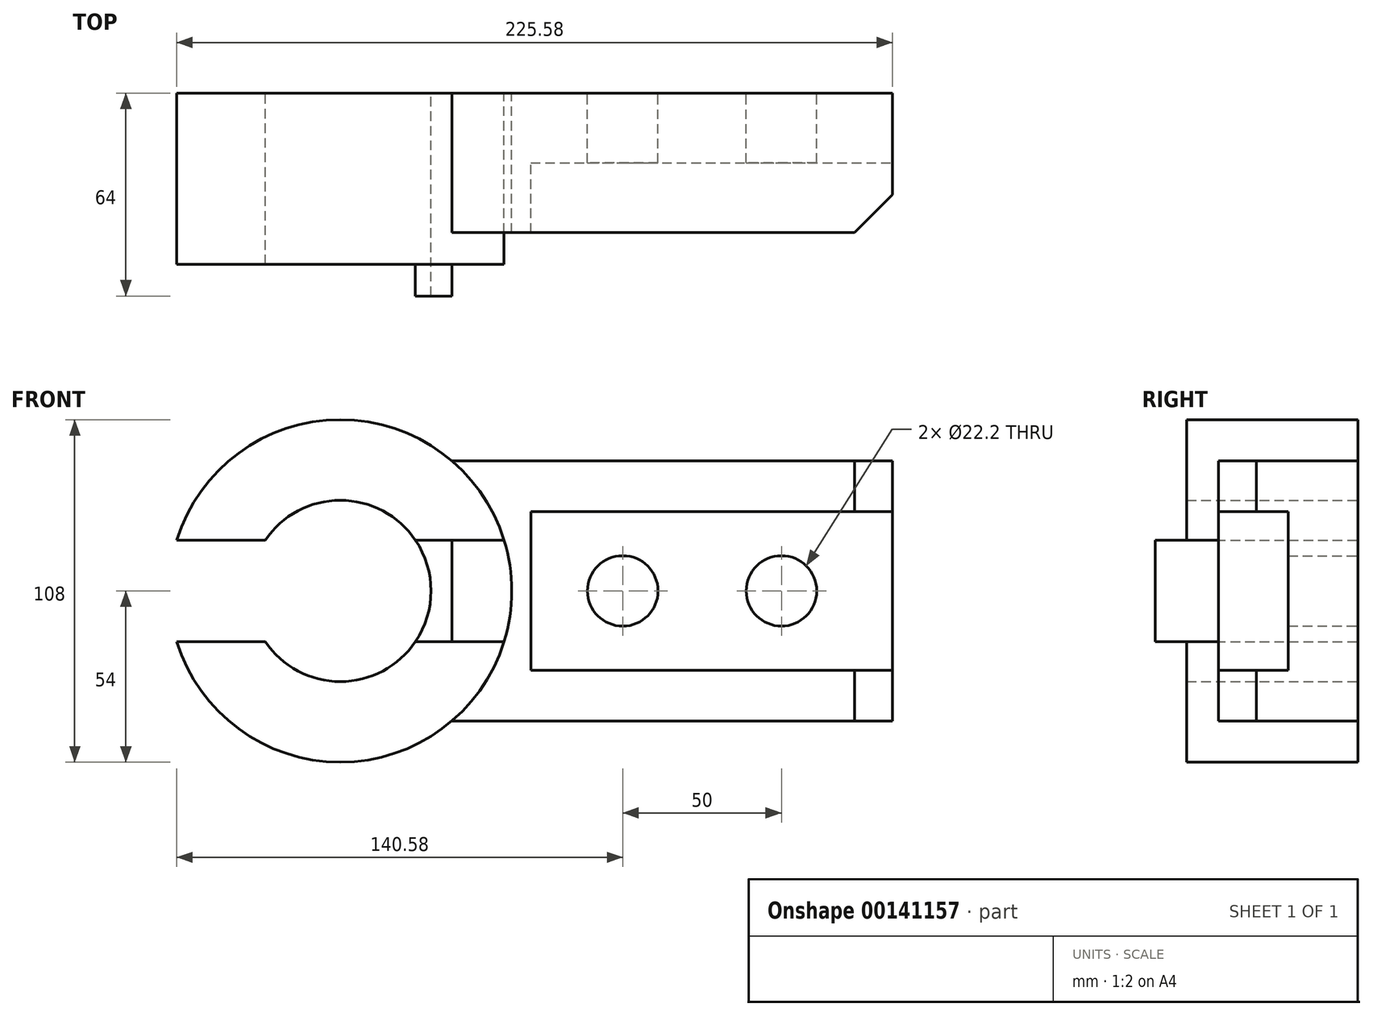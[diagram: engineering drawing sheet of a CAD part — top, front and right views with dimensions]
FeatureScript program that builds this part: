
annotation { "Feature Type Name" : "Feature", "Feature Type Description" : "" }
export const myFeature = defineFeature(function(context is Context, id is Id, definition is map)
    precondition{}
    {
        {
            var Q0;
            Q0=qCreatedBy(makeId("Front.planeOp"),FACE);
            var sketch = newSketch(context, id + "F0", { "sketchPlane" : qUnion([Q0])});
            skCircle(sketch, "E0", {"center": v(0, 41) * mm, "radius": 54 * mm});
            skLineSegment(sketch, "E1.bottom", {"start": v(35.14, 82) * mm, "end": v(174, 82) * mm});
            skLineSegment(sketch, "E1.top", {"start": v(35.14, 0) * mm, "end": v(174, 0) * mm});
            skLineSegment(sketch, "E1.left", {"start": v(35.14, 82) * mm, "end": v(35.14, 0) * mm});
            skLineSegment(sketch, "E1.right", {"start": v(174, 82) * mm, "end": v(174, 0) * mm});
            skCircle(sketch, "E2", {"center": v(0, 41) * mm, "radius": 28.57 * mm});
            skCircle(sketch, "E3", {"center": v(89, 41) * mm, "radius": 11.1 * mm});
            skCircle(sketch, "E4", {"center": v(139, 41) * mm, "radius": 11.1 * mm});
            skLineSegment(sketch, "E5.bottom", {"start": v(-51.58, 57) * mm, "end": v(51.58, 57) * mm});
            skLineSegment(sketch, "E5.top", {"start": v(-51.58, 25) * mm, "end": v(51.58, 25) * mm});
            skArc(sketch, "E6", {"start": v(-51.58, 57) * mm, "mid": v(-54, 41) * mm, "end": v(-51.58, 25) * mm});
            skArc(sketch, "E7", {"start": v(51.58, 25) * mm, "mid": v(54, 41) * mm, "end": v(51.58, 57) * mm});
            skSolve(sketch);
        }
        {
            var Q0;
            {var subQ1=sQuery(id+"F0.wireOp",EDGE,"E1.bottom");Q0=makeQuery(id+"F0.imprint","IMPRINT",FACE,{"disambiguationData":[TD([[makeQuery(id+"F0.imprint","IMPRINT",EDGE,{"derivedFrom":subQ1}),-1.0]])]});}
            extrude(context, id + "F1", {"entities" : qUnion([Q0]), "depth" : 44 * mm});
        }
        {
            var Q0;
            {var subQ0=sQuery(id+"F0.wireOp",EDGE,"E1.left");Q0=makeQuery(id+"F0.imprint","IMPRINT",FACE,{"disambiguationData":[TD([[makeQuery(id+"F0.imprint","IMPRINT",EDGE,{"derivedFrom":subQ0}),-1.0]])]});}
            var Q1;
            {var subQ0=sQuery(id+"F0.wireOp",EDGE,"E1.left");Q1=makeQuery(id+"F0.imprint","IMPRINT",FACE,{"disambiguationData":[TD([[makeQuery(id+"F0.imprint","IMPRINT",EDGE,{"derivedFrom":subQ0}),1.0]])]});}
            var Q2;
            {var subQ0=sQuery(id+"F0.wireOp",EDGE,"E5.bottom");var subQ1=sQuery(id+"F0.wireOp",EDGE,"E0");var subQ2=makeQuery(id+"F0.imprint","INTERSECT",VERTEX,{"disambiguationData":[OD(1.0)],"derivedFrom":[subQ1,subQ0]});Q2=makeQuery(id+"F0.imprint","IMPRINT",FACE,{"disambiguationData":[TD([[makeQuery(id+"F0.imprint","IMPRINT",EDGE,{"disambiguationData":[TD([[subQ2,1.0]])],"derivedFrom":subQ1}),1.0]])]});}
            var Q3;
            {var subQ0=sQuery(id+"F0.wireOp",EDGE,"E5.bottom");var subQ1=sQuery(id+"F0.wireOp",EDGE,"E2");var subQ2=makeQuery(id+"F0.imprint","INTERSECT",VERTEX,{"disambiguationData":[OD(0.0)],"derivedFrom":[subQ1,subQ0]});Q3=makeQuery(id+"F0.imprint","IMPRINT",FACE,{"disambiguationData":[TD([[makeQuery(id+"F0.imprint","IMPRINT",EDGE,{"disambiguationData":[TD([[subQ2,1.0]])],"derivedFrom":subQ1}),-1.0]])]});}
            var Q4;
            {var subQ0=sQuery(id+"F0.wireOp",EDGE,"E5.bottom");var subQ1=sQuery(id+"F0.wireOp",EDGE,"E0");var subQ2=makeQuery(id+"F0.imprint","INTERSECT",VERTEX,{"disambiguationData":[OD(0.0)],"derivedFrom":[subQ1,subQ0]});Q4=makeQuery(id+"F0.imprint","IMPRINT",FACE,{"disambiguationData":[TD([[makeQuery(id+"F0.imprint","IMPRINT",EDGE,{"disambiguationData":[TD([[subQ2,-1.0]])],"derivedFrom":subQ1}),1.0]])]});}
            var Q5;
            {var subQ0=sQuery(id+"F0.wireOp",EDGE,"E5.top");var subQ3=sQuery(id+"F0.wireOp",EDGE,"E2");var subQ4=makeQuery(id+"F0.imprint","INTERSECT",VERTEX,{"disambiguationData":[OD(0.0)],"derivedFrom":[subQ3,subQ0]});Q5=makeQuery(id+"F0.imprint","IMPRINT",FACE,{"disambiguationData":[TD([[makeQuery(id+"F0.imprint","IMPRINT",EDGE,{"disambiguationData":[TD([[subQ4,-1.0]])],"derivedFrom":subQ3}),-1.0]])]});}
            extrude(context, id + "F2", {"entities" : qUnion([Q0, Q1, Q2, Q3, Q4, Q5]), "operationType" : NewBodyOperationType.ADD, "depth" : 64 * mm});
        }
        {
            var Q0;
            Q0=makeQuery(id+"F1.opExtrude","SWEPT_FACE",FACE,{"disambiguationData":[OSD([sQuery(id+"F0.wireOp",EDGE,"E1.bottom")])]});
            var sketch = newSketch(context, id + "F3", { "sketchPlane" : qUnion([Q0])});
            skLineSegment(sketch, "E8", {"start": v(174, -32) * mm, "end": v(162, -44) * mm});
            skLineSegment(sketch, "E9", {"start": v(162, -44) * mm, "end": v(174, -44) * mm});
            skLineSegment(sketch, "E10", {"start": v(174, -44) * mm, "end": v(174, -32) * mm});
            skSolve(sketch);
        }
        {
            var Q0;
            Q0=makeQuery(id+"F1.opExtrude","SWEPT_FACE",FACE,{"disambiguationData":[OSD([sQuery(id+"F0.wireOp",EDGE,"E1.right")])]});
            var sketch = newSketch(context, id + "F4", { "sketchPlane" : qUnion([Q0])});
            skLineSegment(sketch, "E11.bottom", {"start": v(-44, 66) * mm, "end": v(-22, 66) * mm});
            skLineSegment(sketch, "E11.top", {"start": v(-44, 16) * mm, "end": v(-22, 16) * mm});
            skLineSegment(sketch, "E11.left", {"start": v(-44, 66) * mm, "end": v(-44, 16) * mm});
            skLineSegment(sketch, "E11.right", {"start": v(-22, 66) * mm, "end": v(-22, 16) * mm});
            skSolve(sketch);
        }
        {
            var Q0;
            Q0=makeQuery(id+"F4.imprint","IMPRINT",FACE,{"disambiguationData":[TD([[makeQuery(id+"F4.imprint","IMPRINT",EDGE,{"derivedFrom":sQuery(id+"F4.wireOp",EDGE,"E11.bottom")}),-1.0]])]});
            extrude(context, id + "F5", {"entities" : qUnion([Q0]), "operationType" : NewBodyOperationType.REMOVE, "oppositeDirection" : true, "depth" : 114 * mm});
        }
        {
            var Q0;
            Q0=makeQuery(id+"F3.imprint","IMPRINT",FACE,{"disambiguationData":[TD([[makeQuery(id+"F3.imprint","IMPRINT",EDGE,{"derivedFrom":sQuery(id+"F3.wireOp",EDGE,"E8")}),1.0]])]});
            extrude(context, id + "F6", {"entities" : qUnion([Q0]), "operationType" : NewBodyOperationType.REMOVE, "endBound" : BoundingType.THROUGH_ALL, "oppositeDirection" : true, "depth" : 25 * mm});
        }
        {
            var Q0;
            Q0=makeQuery(id+"F2.opExtrude","CAP_FACE",FACE,{"disambiguationData":[OSD([sQuery(id+"F0.wireOp",EDGE,"E0"),sQuery(id+"F0.wireOp",EDGE,"E2")])],"isStart":false});
            var sketch = newSketch(context, id + "F7", { "sketchPlane" : qUnion([Q0])});
            skLineSegment(sketch, "E12.bottom", {"start": v(-51.58, 57) * mm, "end": v(51.58, 57) * mm});
            skLineSegment(sketch, "E12.top", {"start": v(-51.58, 25) * mm, "end": v(51.58, 25) * mm});
            skArc(sketch, "E13", {"start": v(51.58, 57) * mm, "mid": v(0, 95) * mm, "end": v(-51.58, 57) * mm});
            skArc(sketch, "E14", {"start": v(-51.58, 25) * mm, "mid": v(0, -13) * mm, "end": v(51.58, 25) * mm});
            skSolve(sketch);
        }
        {
            var Q0;
            {var subQ0=sQuery(id+"F7.wireOp",EDGE,"E13");Q0=makeQuery(id+"F7.imprint","IMPRINT",FACE,{"disambiguationData":[TD([[makeQuery(id+"F7.imprint","IMPRINT",EDGE,{"derivedFrom":subQ0}),1.0]])]});}
            var Q1;
            {var subQ0=sQuery(id+"F7.wireOp",EDGE,"E14");Q1=makeQuery(id+"F7.imprint","IMPRINT",FACE,{"disambiguationData":[TD([[makeQuery(id+"F7.imprint","IMPRINT",EDGE,{"derivedFrom":subQ0}),1.0]])]});}
            extrude(context, id + "F8", {"entities" : qUnion([Q0, Q1]), "operationType" : NewBodyOperationType.REMOVE, "oppositeDirection" : true, "depth" : 10 * mm});
        }
    });
